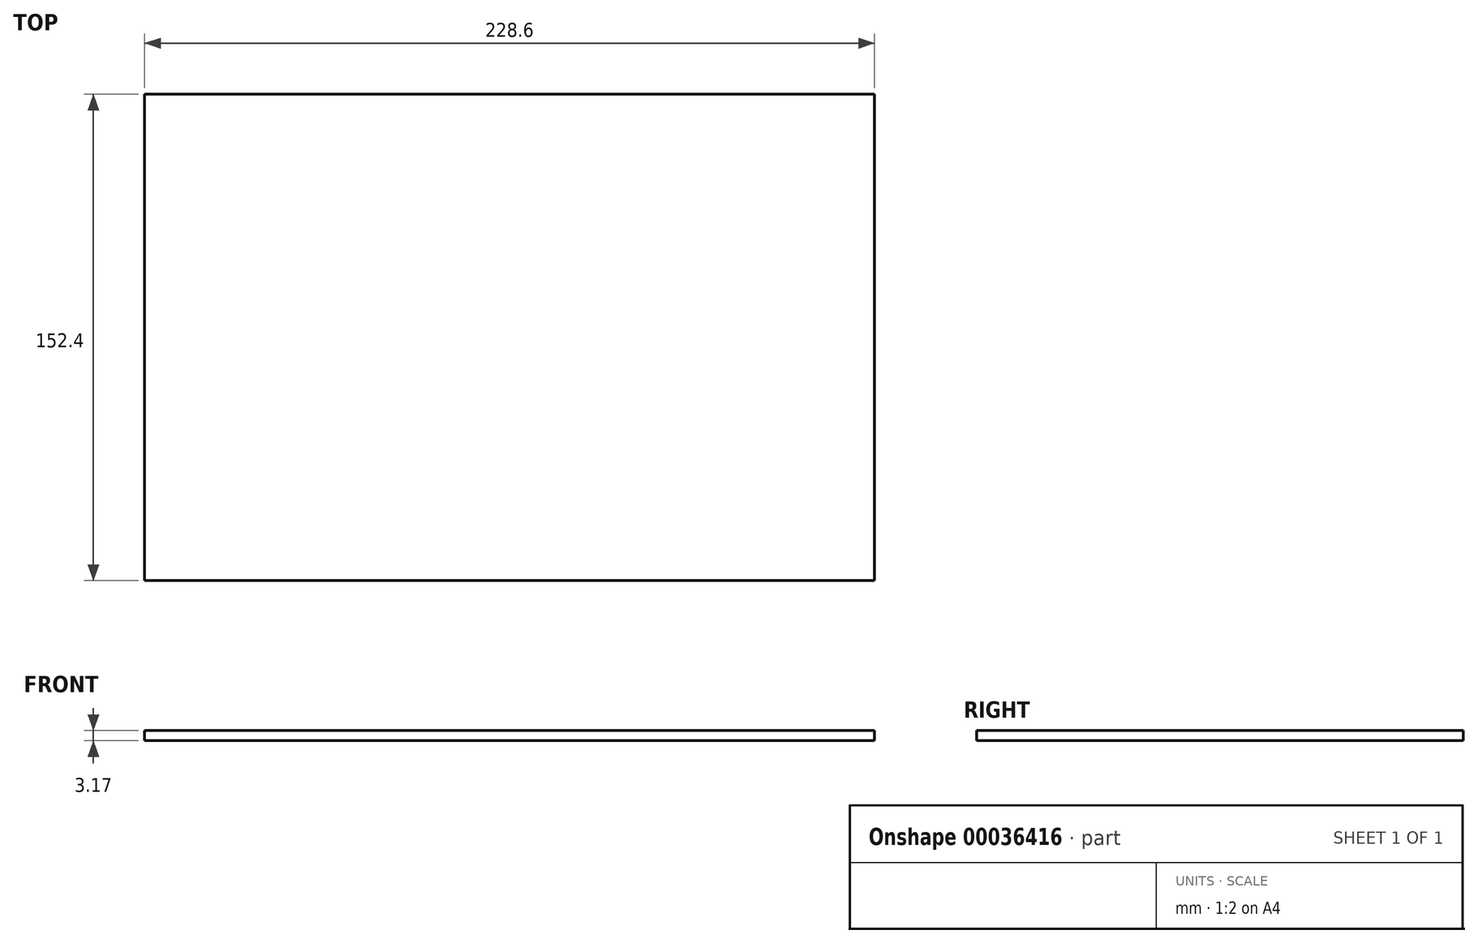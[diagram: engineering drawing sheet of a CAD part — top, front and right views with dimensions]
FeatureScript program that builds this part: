
annotation { "Feature Type Name" : "Feature", "Feature Type Description" : "" }
export const myFeature = defineFeature(function(context is Context, id is Id, definition is map)
    precondition{}
    {
        {
            var Q0;
            Q0=qCreatedBy(makeId("Top.planeOp"),FACE);
            var sketch = newSketch(context, id + "F0", { "sketchPlane" : qUnion([Q0])});
            skLineSegment(sketch, "E0.rect.bottom", {"start": v(114.3, -76.2) * mm, "end": v(-114.3, -76.2) * mm});
            skLineSegment(sketch, "E0.rect.top", {"start": v(114.3, 76.2) * mm, "end": v(-114.3, 76.2) * mm});
            skLineSegment(sketch, "E0.rect.left", {"start": v(114.3, -76.2) * mm, "end": v(114.3, 76.2) * mm});
            skLineSegment(sketch, "E0.rect.right", {"start": v(-114.3, -76.2) * mm, "end": v(-114.3, 76.2) * mm});
            skPoint(sketch, "E0.rect.middle", {"position": v(0, 0) * mm});
            skSolve(sketch);
        }
        {
            var Q0;
            Q0=makeQuery(id+"F0.imprint","IMPRINT",FACE,{"disambiguationData":[TD([[makeQuery(id+"F0.imprint","IMPRINT",EDGE,{"derivedFrom":sQuery(id+"F0.wireOp",EDGE,"E0.rect.bottom")}),-1.0]])]});
            extrude(context, id + "F1", {"entities" : qUnion([Q0]), "depth" : 3.17 * mm});
        }
    });
